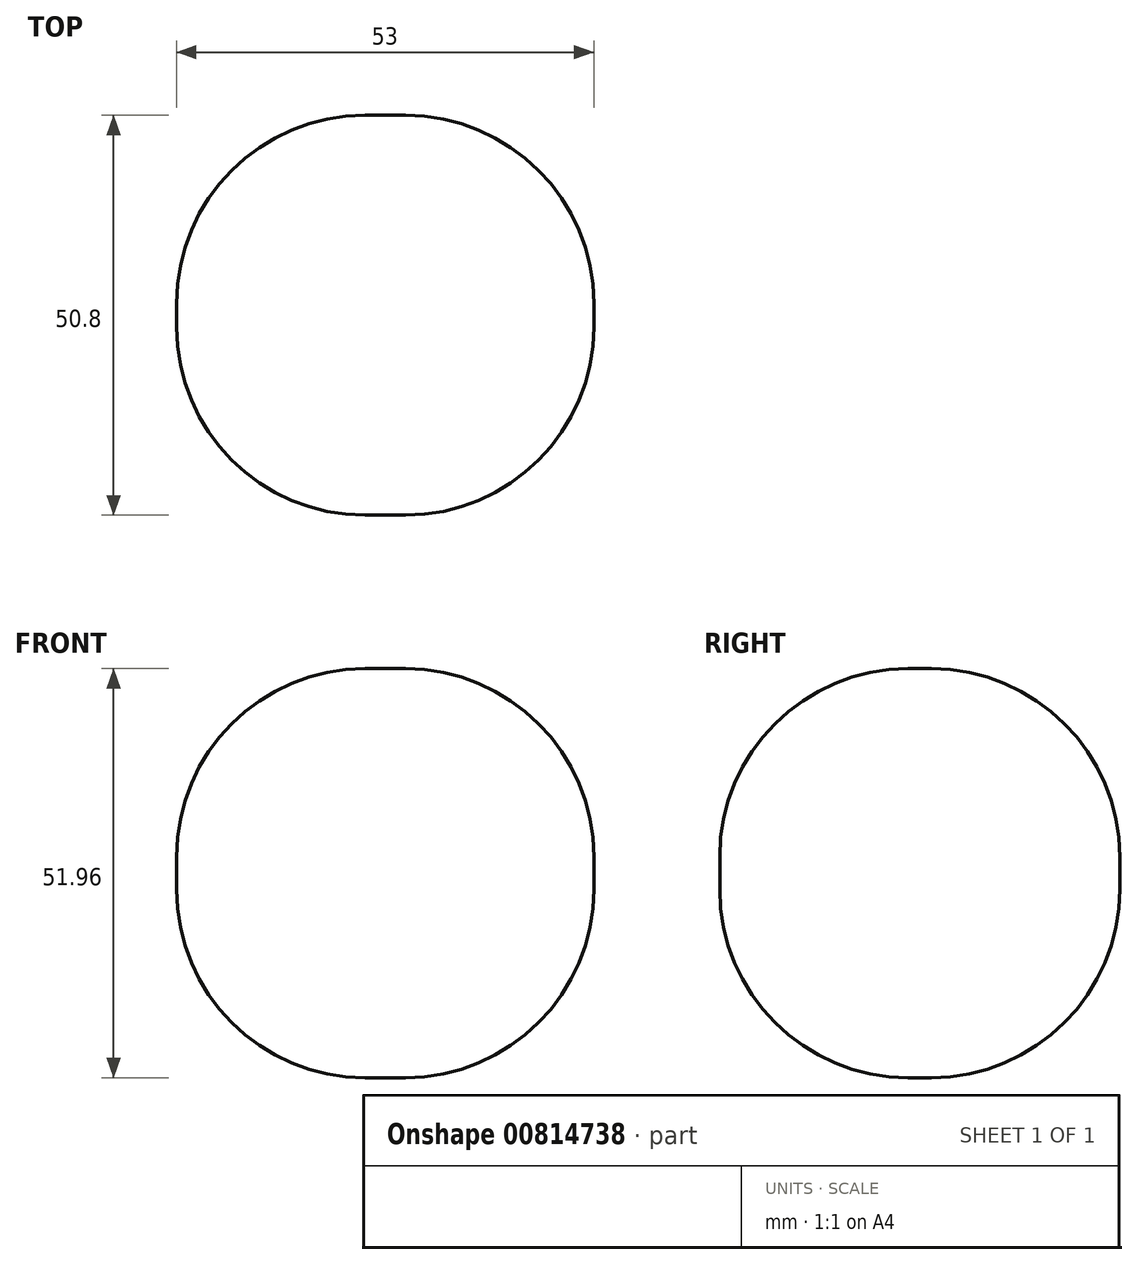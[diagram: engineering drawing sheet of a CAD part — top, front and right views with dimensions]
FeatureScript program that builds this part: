
annotation { "Feature Type Name" : "Feature", "Feature Type Description" : "" }
export const myFeature = defineFeature(function(context is Context, id is Id, definition is map)
    precondition{}
    {
        {
            var Q0;
            Q0=qCreatedBy(makeId("Front.planeOp"),FACE);
            var sketch = newSketch(context, id + "F0", { "sketchPlane" : qUnion([Q0])});
            skLineSegment(sketch, "E0.bottom", {"start": v(26.5, 24.03) * mm, "end": v(-26.5, 24.03) * mm});
            skLineSegment(sketch, "E0.top", {"start": v(26.5, -27.93) * mm, "end": v(-26.5, -27.93) * mm});
            skLineSegment(sketch, "E0.left", {"start": v(26.5, 24.03) * mm, "end": v(26.5, -27.93) * mm});
            skLineSegment(sketch, "E0.right", {"start": v(-26.5, 24.03) * mm, "end": v(-26.5, -27.93) * mm});
            skPoint(sketch, "E0.middle", {"position": v(0, -1.95) * mm});
            skSolve(sketch);
        }
        {
            var Q0;
            Q0=makeQuery(id+"F0.imprint","IMPRINT",FACE,{"disambiguationData":[TD([[makeQuery(id+"F0.imprint","IMPRINT",EDGE,{"derivedFrom":sQuery(id+"F0.wireOp",EDGE,"E0.bottom")}),1.0]])]});
            extrude(context, id + "F1", {"entities" : qUnion([Q0]), "depth" : 50.8 * mm, "offsetDistance" : 25.4 * mm});
        }
        {
            var Q0;
            Q0=makeQuery(id+"F1.opExtrude","SWEPT_FACE",FACE,{"disambiguationData":[OSD([sQuery(id+"F0.wireOp",EDGE,"E0.bottom")])]});
            var Q1;
            Q1=makeQuery(id+"F1.opExtrude","SWEPT_FACE",FACE,{"disambiguationData":[OSD([sQuery(id+"F0.wireOp",EDGE,"E0.right")])]});
            var Q2;
            Q2=makeQuery(id+"F1.opExtrude","CAP_FACE",FACE,{"disambiguationData":[OSD([sQuery(id+"F0.wireOp",EDGE,"E0.bottom"),sQuery(id+"F0.wireOp",EDGE,"E0.top"),sQuery(id+"F0.wireOp",EDGE,"E0.left"),sQuery(id+"F0.wireOp",EDGE,"E0.right")])],"isStart":false});
            var Q3;
            Q3=makeQuery(id+"F1.opExtrude","SWEPT_FACE",FACE,{"disambiguationData":[OSD([sQuery(id+"F0.wireOp",EDGE,"E0.left")])]});
            var Q4;
            Q4=makeQuery(id+"F1.opExtrude","CAP_FACE",FACE,{"disambiguationData":[OSD([sQuery(id+"F0.wireOp",EDGE,"E0.bottom"),sQuery(id+"F0.wireOp",EDGE,"E0.top"),sQuery(id+"F0.wireOp",EDGE,"E0.left"),sQuery(id+"F0.wireOp",EDGE,"E0.right")])],"isStart":true});
            var Q5;
            Q5=makeQuery(id+"F1.opExtrude","SWEPT_FACE",FACE,{"disambiguationData":[OSD([sQuery(id+"F0.wireOp",EDGE,"E0.top")])]});
            fillet(context, id + "F2", {"entities" : qUnion([Q0, Q1, Q2, Q3, Q4, Q5]), "radius" : 23.92 * mm, "tangentPropagation" : true, "allowEdgeOverflow" : false});
        }
    });
